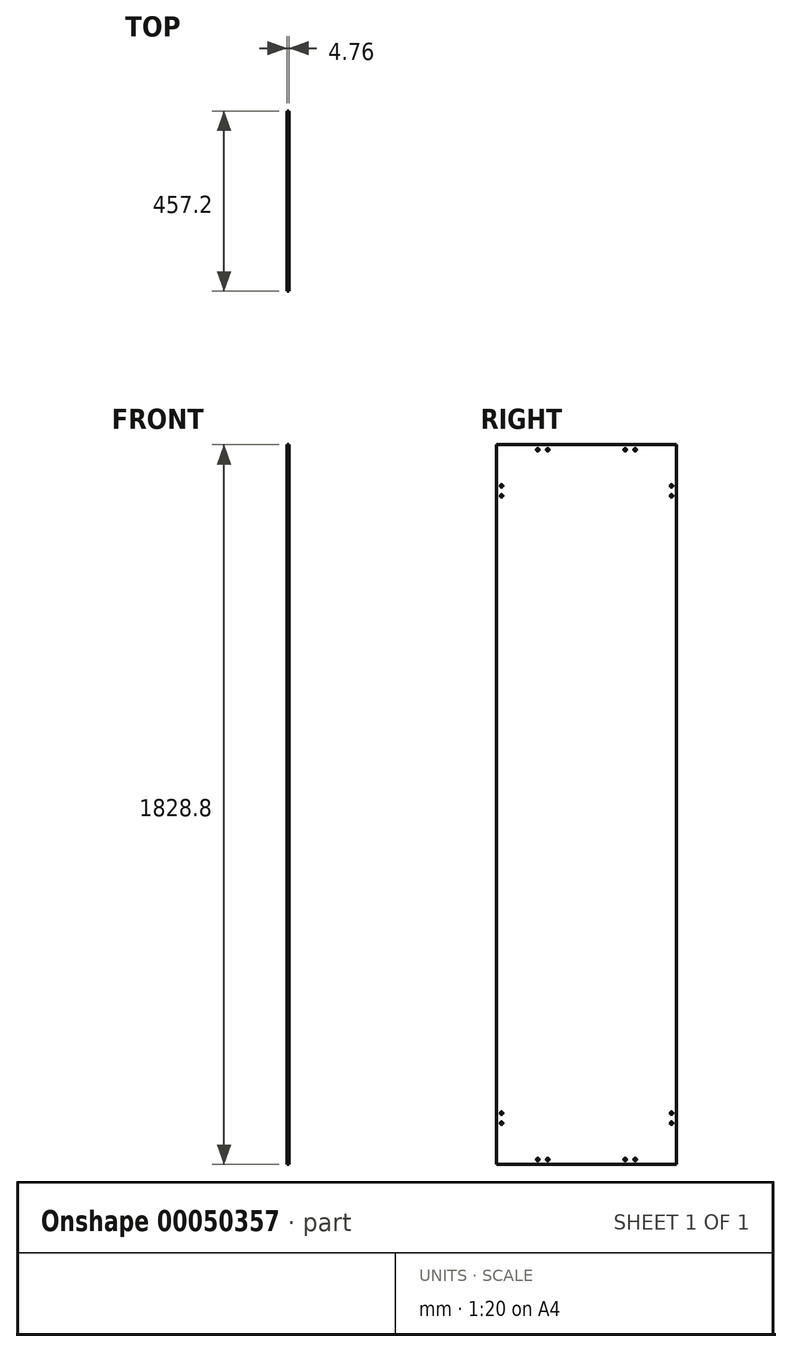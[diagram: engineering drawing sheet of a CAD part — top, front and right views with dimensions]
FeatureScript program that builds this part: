
annotation { "Feature Type Name" : "Feature", "Feature Type Description" : "" }
export const myFeature = defineFeature(function(context is Context, id is Id, definition is map)
    precondition{}
    {
        {
            var Q0;
            Q0=qCreatedBy(makeId("Right.planeOp"),FACE);
            var sketch = newSketch(context, id + "F0", { "sketchPlane" : qUnion([Q0])});
            skLineSegment(sketch, "E0.rect.bottom", {"start": v(-858.72, -877.41) * mm, "end": v(-1315.92, -877.41) * mm});
            skLineSegment(sketch, "E0.rect.top", {"start": v(-858.72, 951.39) * mm, "end": v(-1315.92, 951.39) * mm});
            skLineSegment(sketch, "E0.rect.left", {"start": v(-858.72, -877.41) * mm, "end": v(-858.72, 951.39) * mm});
            skLineSegment(sketch, "E0.rect.right", {"start": v(-1315.92, -877.41) * mm, "end": v(-1315.92, 951.39) * mm});
            skPoint(sketch, "E0.rect.middle", {"position": v(-1087.32, 36.99) * mm});
            skSolve(sketch);
        }
        {
            var Q0;
            Q0=makeQuery(id+"F0.imprint","IMPRINT",FACE,{"disambiguationData":[TD([[makeQuery(id+"F0.imprint","IMPRINT",EDGE,{"derivedFrom":sQuery(id+"F0.wireOp",EDGE,"E0.rect.bottom")}),-1.0]])]});
            extrude(context, id + "F1", {"entities" : qUnion([Q0]), "depth" : 4.76 * mm});
        }
        {
            var Q0;
            Q0=makeQuery(id+"F1.opExtrude","CAP_FACE",FACE,{"disambiguationData":[OSD([sQuery(id+"F0.wireOp",EDGE,"E0.rect.bottom"),sQuery(id+"F0.wireOp",EDGE,"E0.rect.top"),sQuery(id+"F0.wireOp",EDGE,"E0.rect.left"),sQuery(id+"F0.wireOp",EDGE,"E0.rect.right")])],"isStart":false});
            var sketch = newSketch(context, id + "F2", { "sketchPlane" : qUnion([Q0])});
            skCircle(sketch, "E1", {"center": v(-1303.22, 846.61) * mm, "radius": 3.18 * mm});
            skCircle(sketch, "E2", {"center": v(-1303.22, 821.21) * mm, "radius": 3.18 * mm});
            skCircle(sketch, "E3", {"center": v(-1211.15, 938.69) * mm, "radius": 3.18 * mm});
            skCircle(sketch, "E4", {"center": v(-1185.75, 938.69) * mm, "radius": 3.18 * mm});
            skSolve(sketch);
        }
        {
            var Q0;
            Q0=makeQuery(id+"F2.imprint","IMPRINT",FACE,{"disambiguationData":[TD([[makeQuery(id+"F2.imprint","IMPRINT",EDGE,{"derivedFrom":sQuery(id+"F2.wireOp",EDGE,"E1")}),-1.0]])]});
            var sketch = newSketch(context, id + "F3", { "sketchPlane" : qUnion([Q0])});
            skCircle(sketch, "E5", {"center": v(-988.9, 938.69) * mm, "radius": 3.18 * mm});
            skCircle(sketch, "E6", {"center": v(-963.5, 938.69) * mm, "radius": 3.18 * mm});
            skCircle(sketch, "E7", {"center": v(-871.42, 846.61) * mm, "radius": 3.18 * mm});
            skCircle(sketch, "E8", {"center": v(-871.42, 821.21) * mm, "radius": 3.18 * mm});
            skSolve(sketch);
        }
        {
            var Q0;
            Q0=makeQuery(id+"F3.imprint","IMPRINT",FACE,{"disambiguationData":[TD([[makeQuery(id+"F3.imprint","IMPRINT",EDGE,{"derivedFrom":sQuery(id+"F3.wireOp",EDGE,"E5")}),-1.0]])]});
            var sketch = newSketch(context, id + "F4", { "sketchPlane" : qUnion([Q0])});
            skCircle(sketch, "E9", {"center": v(-871.42, -772.64) * mm, "radius": 3.18 * mm});
            skCircle(sketch, "E10", {"center": v(-871.42, -747.24) * mm, "radius": 3.18 * mm});
            skCircle(sketch, "E11", {"center": v(-963.5, -864.71) * mm, "radius": 3.18 * mm});
            skCircle(sketch, "E12", {"center": v(-988.9, -864.71) * mm, "radius": 3.18 * mm});
            skSolve(sketch);
        }
        {
            var Q0;
            Q0=makeQuery(id+"F2.imprint","IMPRINT",FACE,{"disambiguationData":[TD([[makeQuery(id+"F2.imprint","IMPRINT",EDGE,{"derivedFrom":sQuery(id+"F2.wireOp",EDGE,"E1")}),-1.0]])]});
            var sketch = newSketch(context, id + "F5", { "sketchPlane" : qUnion([Q0])});
            skCircle(sketch, "E13", {"center": v(-1303.22, -772.64) * mm, "radius": 3.18 * mm});
            skCircle(sketch, "E14", {"center": v(-1303.22, -747.24) * mm, "radius": 3.18 * mm});
            skCircle(sketch, "E15", {"center": v(-1211.15, -864.71) * mm, "radius": 3.18 * mm});
            skCircle(sketch, "E16", {"center": v(-1185.75, -864.71) * mm, "radius": 3.18 * mm});
            skSolve(sketch);
        }
        {
            var Q0;
            Q0 = qSketchRegion(id + "F2", true);
            var Q1;
            Q1 = qSketchRegion(id + "F3", true);
            var Q2;
            Q2 = qSketchRegion(id + "F4", true);
            var Q3;
            Q3 = qSketchRegion(id + "F5", true);
            extrude(context, id + "F6", {"entities" : qUnion([Q0, Q1, Q2, Q3]), "operationType" : NewBodyOperationType.REMOVE, "oppositeDirection" : true, "depth" : 25.4 * mm});
        }
    });
